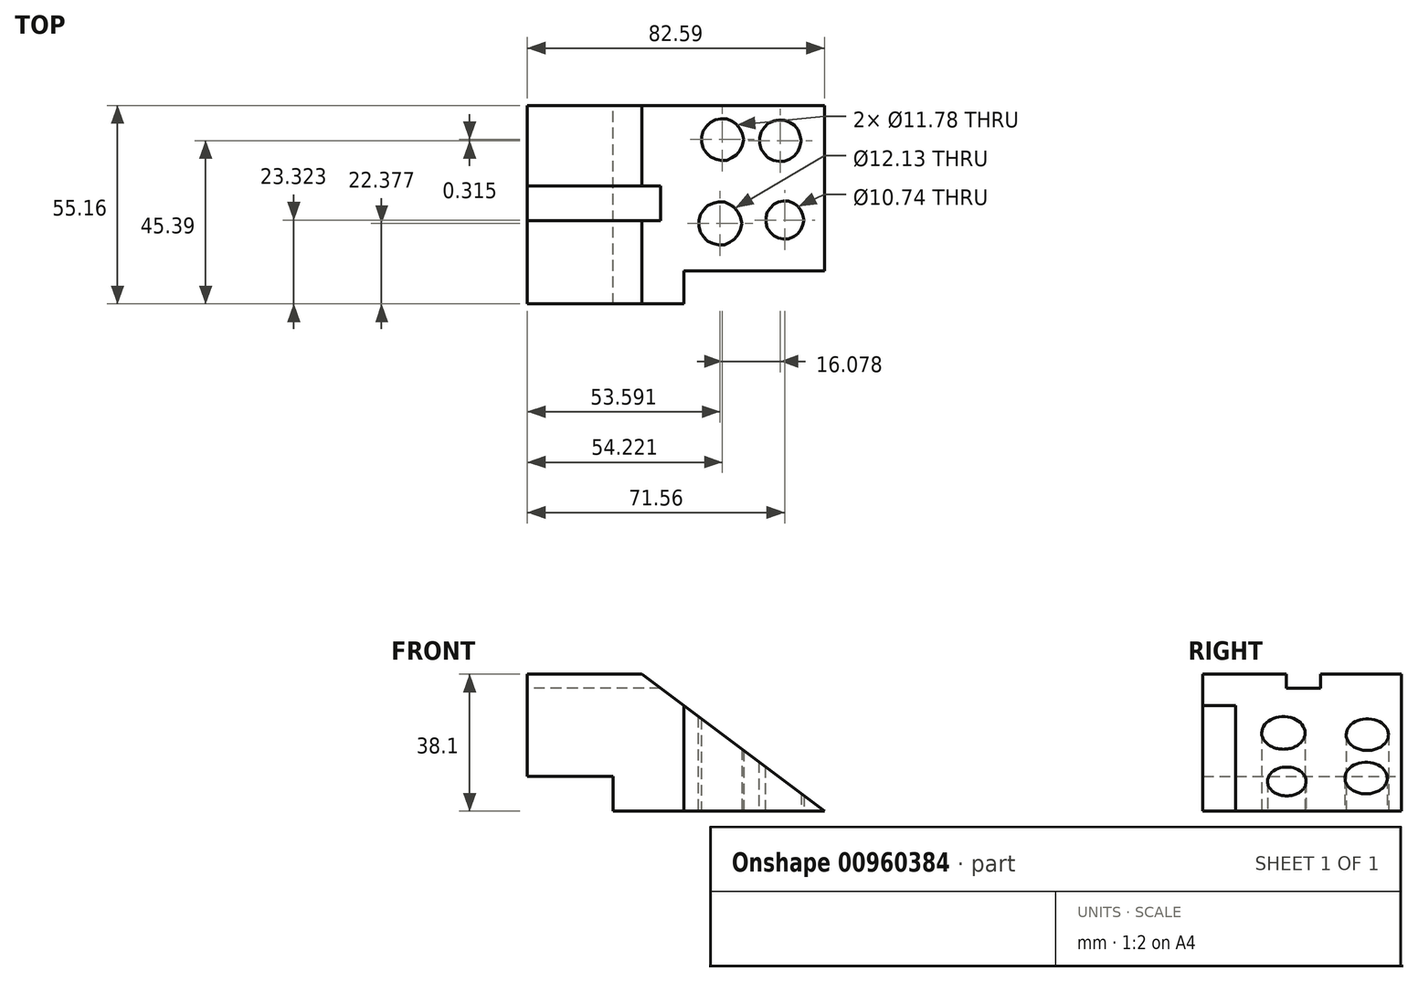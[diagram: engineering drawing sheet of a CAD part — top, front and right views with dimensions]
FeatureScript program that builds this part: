
annotation { "Feature Type Name" : "Feature", "Feature Type Description" : "" }
export const myFeature = defineFeature(function(context is Context, id is Id, definition is map)
    precondition{}
    {
        {
            var Q0;
            Q0=qCreatedBy(makeId("Top.planeOp"),FACE);
            var sketch = newSketch(context, id + "F0", { "sketchPlane" : qUnion([Q0])});
            skLineSegment(sketch, "E0", {"start": v(-48.71, 24.63) * mm, "end": v(-48.71, -30.53) * mm});
            skLineSegment(sketch, "E1", {"start": v(-48.71, -30.53) * mm, "end": v(-5.2, -30.53) * mm});
            skLineSegment(sketch, "E2", {"start": v(-5.2, -30.53) * mm, "end": v(-5.2, -21.4) * mm});
            skLineSegment(sketch, "E3", {"start": v(-5.2, -21.4) * mm, "end": v(33.88, -21.4) * mm});
            skLineSegment(sketch, "E4", {"start": v(33.88, -21.4) * mm, "end": v(33.88, 24.63) * mm});
            skLineSegment(sketch, "E5", {"start": v(33.88, 24.63) * mm, "end": v(-48.71, 24.63) * mm});
            skCircle(sketch, "E6", {"center": v(4.88, -8.15) * mm, "radius": 6.06 * mm});
            skCircle(sketch, "E7", {"center": v(22.85, -7.2) * mm, "radius": 5.37 * mm});
            skCircle(sketch, "E8", {"center": v(5.51, 15.18) * mm, "radius": 5.89 * mm});
            skCircle(sketch, "E9", {"center": v(21.59, 14.86) * mm, "radius": 5.89 * mm});
            skSolve(sketch);
        }
        {
            var Q0;
            Q0=makeQuery(id+"F0.imprint","IMPRINT",FACE,{"disambiguationData":[TD([[makeQuery(id+"F0.imprint","IMPRINT",EDGE,{"derivedFrom":sQuery(id+"F0.wireOp",EDGE,"E0")}),1.0]])]});
            extrude(context, id + "F1", {"entities" : qUnion([Q0]), "depth" : 38.1 * mm, "offsetDistance" : 25.4 * mm});
        }
        {
            var Q0;
            Q0=makeQuery(id+"F1.opExtrude","SWEPT_FACE",FACE,{"disambiguationData":[OSD([sQuery(id+"F0.wireOp",EDGE,"E5")])]});
            var sketch = newSketch(context, id + "F2", { "sketchPlane" : qUnion([Q0])});
            skLineSegment(sketch, "E10", {"start": v(16.87, 38.1) * mm, "end": v(-33.88, 0) * mm});
            skLineSegment(sketch, "E11", {"start": v(-33.88, 0) * mm, "end": v(-33.88, 38.1) * mm});
            skLineSegment(sketch, "E12", {"start": v(-33.88, 38.1) * mm, "end": v(16.87, 38.1) * mm});
            skLineSegment(sketch, "E13.bottom", {"start": v(48.71, 0) * mm, "end": v(24.9, 0) * mm});
            skLineSegment(sketch, "E13.top", {"start": v(48.71, 9.72) * mm, "end": v(24.9, 9.72) * mm});
            skLineSegment(sketch, "E13.left", {"start": v(48.71, 0) * mm, "end": v(48.71, 9.72) * mm});
            skLineSegment(sketch, "E13.right", {"start": v(24.9, 0) * mm, "end": v(24.9, 9.72) * mm});
            skSolve(sketch);
        }
        {
            var Q0;
            Q0=makeQuery(id+"F2.imprint","IMPRINT",FACE,{"disambiguationData":[TD([[makeQuery(id+"F2.imprint","IMPRINT",EDGE,{"derivedFrom":sQuery(id+"F2.wireOp",EDGE,"E10")}),-1.0]])]});
            var Q1;
            Q1=makeQuery(id+"F2.imprint","IMPRINT",FACE,{"disambiguationData":[TD([[makeQuery(id+"F2.imprint","IMPRINT",EDGE,{"derivedFrom":sQuery(id+"F2.wireOp",EDGE,"E13.bottom")}),1.0]])]});
            var Q2;
            Q2=makeQuery(id+"F1.opExtrude","SWEPT_FACE",FACE,{"disambiguationData":[OSD([sQuery(id+"F0.wireOp",EDGE,"E1")])]});
            extrude(context, id + "F3", {"entities" : qUnion([Q0, Q1]), "operationType" : NewBodyOperationType.REMOVE, "endBound" : BoundingType.UP_TO_SURFACE, "oppositeDirection" : true, "depth" : 25.4 * mm, "endBoundEntityFace" : qUnion([Q2]), "offsetDistance" : 25.4 * mm});
        }
        {
            var Q0;
            Q0=makeQuery(id+"F1.opExtrude","SWEPT_FACE",FACE,{"disambiguationData":[OSD([sQuery(id+"F0.wireOp",EDGE,"E0")])]});
            var sketch = newSketch(context, id + "F4", { "sketchPlane" : qUnion([Q0])});
            skLineSegment(sketch, "E14", {"start": v(-2.23, 38.1) * mm, "end": v(-2.23, 34.2) * mm});
            skLineSegment(sketch, "E15", {"start": v(-2.23, 34.2) * mm, "end": v(7.38, 34.2) * mm});
            skLineSegment(sketch, "E16", {"start": v(7.38, 34.2) * mm, "end": v(7.38, 38.1) * mm});
            skLineSegment(sketch, "E17", {"start": v(7.38, 38.1) * mm, "end": v(-2.23, 38.1) * mm});
            skSolve(sketch);
        }
        {
            var Q0;
            Q0=makeQuery(id+"F4.imprint","IMPRINT",FACE,{"disambiguationData":[TD([[makeQuery(id+"F4.imprint","IMPRINT",EDGE,{"derivedFrom":sQuery(id+"F4.wireOp",EDGE,"E14")}),1.0]])]});
            extrude(context, id + "F5", {"entities" : qUnion([Q0]), "operationType" : NewBodyOperationType.REMOVE, "endBound" : BoundingType.THROUGH_ALL, "oppositeDirection" : true, "depth" : 25.4 * mm, "offsetDistance" : 25.4 * mm});
        }
    });
